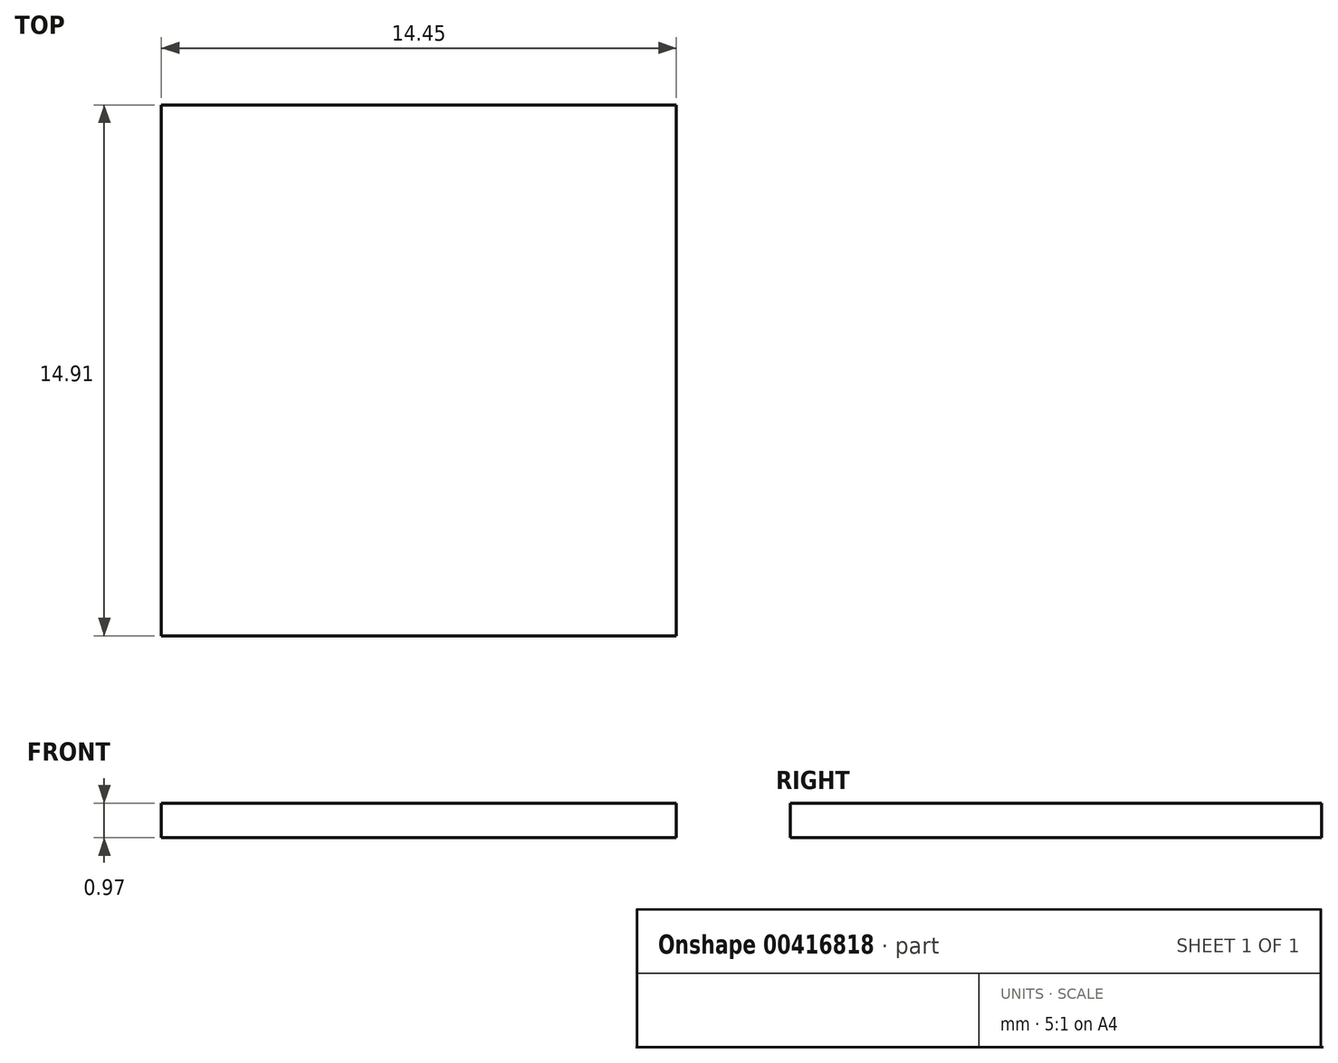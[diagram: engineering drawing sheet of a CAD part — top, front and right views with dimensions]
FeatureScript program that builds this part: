
annotation { "Feature Type Name" : "Feature", "Feature Type Description" : "" }
export const myFeature = defineFeature(function(context is Context, id is Id, definition is map)
    precondition{}
    {
        {
            var Q0;
            Q0=qCreatedBy(makeId("Top.planeOp"),FACE);
            var sketch = newSketch(context, id + "F0", { "sketchPlane" : qUnion([Q0])});
            skLineSegment(sketch, "E0.bottom", {"start": v(0, 0) * mm, "end": v(14.45, 0) * mm});
            skLineSegment(sketch, "E0.top", {"start": v(0, 14.9) * mm, "end": v(14.45, 14.9) * mm});
            skLineSegment(sketch, "E0.left", {"start": v(0, 0) * mm, "end": v(0, 14.9) * mm});
            skLineSegment(sketch, "E0.right", {"start": v(14.45, 0) * mm, "end": v(14.45, 14.9) * mm});
            skSolve(sketch);
        }
        {
            var Q0;
            Q0 = qSketchRegion(id + "F0", true);
            extrude(context, id + "F1", {"entities" : qUnion([Q0]), "depth" : .97 * mm, "offsetDistance" : 25.4 * mm});
        }
    });
